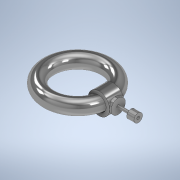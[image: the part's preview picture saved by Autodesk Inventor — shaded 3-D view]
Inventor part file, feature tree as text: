
AUTODESK INVENTOR PART (.ipt)
format: ipt  version: 2021 (Build 250183000, 183)  size: 227,840 bytes
history: native  units: in
note: dims shown in document units (in); Inventor stores cm internally (conversion verified against a paired STEP export)
features: extrude x5, other x4, sketch x2, revolve x1, plane x1
ambient origin geometry x8: Origin, YZ Plane, XZ Plane, XY Plane, X Axis, Y Axis, Z Axis, Center Point
bodies: Solid1 (feature_tree)
feature tree (13):
  sketch  "Sketch1"  dims[d0=0.0394in d1=0.0787in]
  revolve  "Revolution1"  [1 undecoded]
  extrude  "Extrusion1"  Depth=0.0591in
  plane  "Work Plane1"
  sketch  "Sketch2"  dims[d2=90.0deg d3=0.0591in d4=0.0394in d5=0.0in d6=0.0394in d7=0.0236in d8=0.0079in d9=0.0079in d10=0.0in d11=0.0394in d12=0.0in d13=0.0197in d14=0.0in d15=0.0039in d16=0.0in d17=0.7874in d18=0.3937in d19=0.3937in d20=0.5906in d21=0.3937in d22=0.3937in]
  extrude  "Extrusion2"  Depth=0.3937in TaperAngle=0.0deg
  extrude  "Extrusion3"  Depth=0.3937in
  extrude  "Extrusion4"  Depth=0.3937in
  extrude  "Extrusion5"  Depth=0.3937in
  other  "Edição direta1"
  other  "Edição direta2"
  other  "Escala1"
  other  "Escala2"
note: 1 required parameter value undecoded (feature->parameter linkage not recoverable at this tier; creation-order binding heuristic only, values carry confidence <= 0.55)
